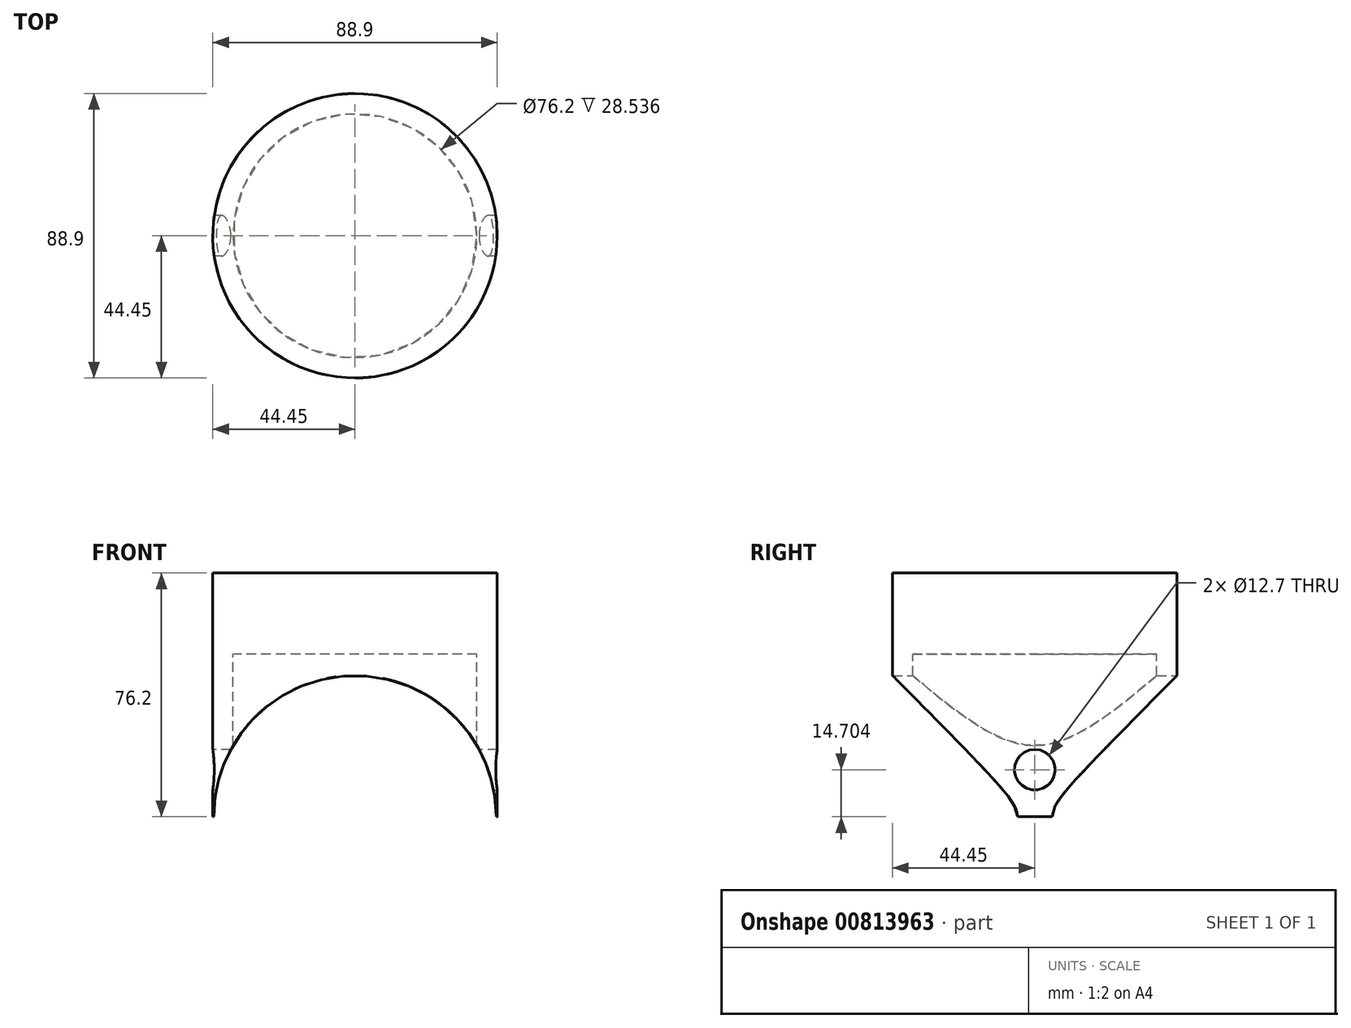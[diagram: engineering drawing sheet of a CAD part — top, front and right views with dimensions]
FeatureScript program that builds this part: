
annotation { "Feature Type Name" : "Feature", "Feature Type Description" : "" }
export const myFeature = defineFeature(function(context is Context, id is Id, definition is map)
    precondition{}
    {
        {
            var Q0;
            Q0=qCreatedBy(makeId("Top.planeOp"),FACE);
            var sketch = newSketch(context, id + "F0", { "sketchPlane" : qUnion([Q0])});
            skCircle(sketch, "E0", {"center": v(0, 0) * mm, "radius": 38.1 * mm});
            skCircle(sketch, "E1", {"center": v(0, 0) * mm, "radius": 44.45 * mm});
            skSolve(sketch);
        }
        {
            var Q0;
            Q0=makeQuery(id+"F0.imprint","IMPRINT",FACE,{"disambiguationData":[TD([[makeQuery(id+"F0.imprint","IMPRINT",EDGE,{"derivedFrom":sQuery(id+"F0.wireOp",EDGE,"E0")}),-1.0]])]});
            var Q1;
            Q1=makeQuery(id+"F0.imprint","IMPRINT",FACE,{"disambiguationData":[TD([[makeQuery(id+"F0.imprint","IMPRINT",EDGE,{"derivedFrom":sQuery(id+"F0.wireOp",EDGE,"E0")}),1.0]])]});
            extrude(context, id + "F1", {"entities" : qUnion([Q0, Q1]), "depth" : 25.4 * mm, "offsetDistance" : 25.4 * mm});
        }
        {
            var Q0;
            Q0=makeQuery(id+"F0.imprint","IMPRINT",FACE,{"disambiguationData":[TD([[makeQuery(id+"F0.imprint","IMPRINT",EDGE,{"derivedFrom":sQuery(id+"F0.wireOp",EDGE,"E0")}),-1.0]])]});
            extrude(context, id + "F2", {"entities" : qUnion([Q0]), "operationType" : NewBodyOperationType.ADD, "oppositeDirection" : true, "depth" : 50.8 * mm, "offsetDistance" : 25.4 * mm});
        }
        {
            var Q0;
            Q0=qCreatedBy(makeId("Front.planeOp"),FACE);
            var sketch = newSketch(context, id + "F3", { "sketchPlane" : qUnion([Q0])});
            skCircle(sketch, "E2", {"center": v(0, -50.77) * mm, "radius": 44.12 * mm});
            skSolve(sketch);
        }
        {
            var Q0;
            Q0=makeQuery(id+"F3.imprint","IMPRINT",FACE,{"disambiguationData":[TD([[makeQuery(id+"F3.imprint","IMPRINT",EDGE,{"derivedFrom":sQuery(id+"F3.wireOp",EDGE,"E2")}),1.0]])]});
            extrude(context, id + "F4", {"entities" : qUnion([Q0]), "operationType" : NewBodyOperationType.REMOVE, "depth" : 60.45 * mm, "offsetDistance" : 25.4 * mm, "hasSecondDirection" : true, "secondDirectionOppositeDirection" : true, "secondDirectionDepth" : 62.74 * mm});
        }
        {
            var Q0;
            Q0=qCreatedBy(makeId("Right.planeOp"),FACE);
            var sketch = newSketch(context, id + "F5", { "sketchPlane" : qUnion([Q0])});
            skCircle(sketch, "E3", {"center": v(0, -36.1) * mm, "radius": 6.35 * mm});
            skSolve(sketch);
        }
        {
            var Q0;
            Q0=makeQuery(id+"F5.imprint","IMPRINT",FACE,{"disambiguationData":[TD([[makeQuery(id+"F5.imprint","IMPRINT",EDGE,{"derivedFrom":sQuery(id+"F5.wireOp",EDGE,"E3")}),1.0]])]});
            extrude(context, id + "F6", {"entities" : qUnion([Q0]), "operationType" : NewBodyOperationType.REMOVE, "depth" : 56.13 * mm, "offsetDistance" : 25.4 * mm, "hasSecondDirection" : true, "secondDirectionOppositeDirection" : true, "secondDirectionDepth" : 57.66 * mm});
        }
    });
